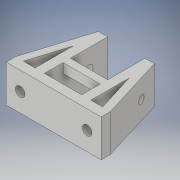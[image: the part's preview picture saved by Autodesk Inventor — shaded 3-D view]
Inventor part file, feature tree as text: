
AUTODESK INVENTOR PART (.ipt)
format: ipt  version: 2018 (Build 220112000, 112)  size: 153,600 bytes
history: native  units: in
note: dims shown in document units (in); Inventor stores cm internally (conversion verified against a paired STEP export)
features: extrude x5, sketch x5
ambient origin geometry x8: Origin, YZ Plane, XZ Plane, XY Plane, X Axis, Y Axis, Z Axis, Center Point
bodies: Solid1 (feature_tree)
feature tree (10):
  extrude  "Extrusion1"  Depth=0.7874in
  extrude  "Extrusion2"  Depth=0.7874in
  extrude  "Extrusion3"  Depth=0.1969in
  extrude  "Extrusion4"  Depth=0.1575in
  extrude  "Extrusion6"  Depth=0.1969in TaperAngle=0.0deg
  sketch  "Sketch1"  dims[d0=2.0079in d1=0.7874in]
  sketch  "Sketch2"  dims[d2=0.1969in d3=0.0in d4=0.7874in]
  sketch  "Sketch3"  dims[d5=0.1969in d6=0.1969in]
  sketch  "Sketch4"  dims[d7=1.3386in d8=0.1575in]
  sketch  "Sketch6"  dims[d9=0.1575in d10=0.1969in d11=0.0in d12=0.1654in d13=0.3937in d14=1.5748in d15=0.0in d16=1.5748in d17=0.0in d18=0.7874in d19=0.1575in d20=0.1969in d21=0.0in d25=0.2047in d26=0.7087in d27=0.7087in d28=0.1969in d29=0.0in]
